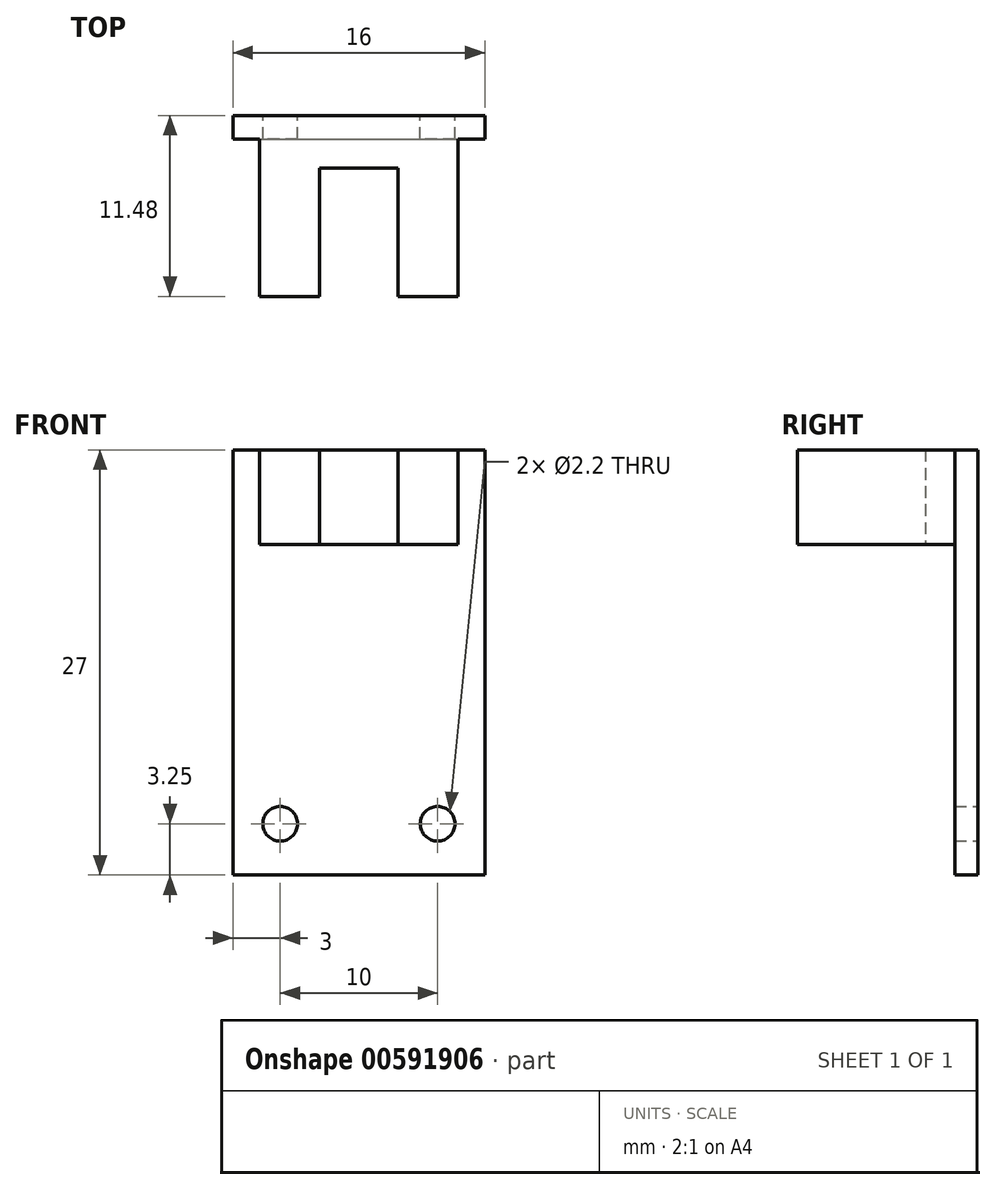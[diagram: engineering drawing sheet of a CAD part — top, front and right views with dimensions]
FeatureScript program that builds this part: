
annotation { "Feature Type Name" : "Feature", "Feature Type Description" : "" }
export const myFeature = defineFeature(function(context is Context, id is Id, definition is map)
    precondition{}
    {
        {
            var Q0;
            Q0=qCreatedBy(makeId("Front.planeOp"),FACE);
            var sketch = newSketch(context, id + "F0", { "sketchPlane" : qUnion([Q0])});
            skLineSegment(sketch, "E0.bottom", {"start": v(0, 0) * mm, "end": v(16, 0) * mm});
            skLineSegment(sketch, "E0.top", {"start": v(0, -27) * mm, "end": v(16, -27) * mm});
            skLineSegment(sketch, "E0.left", {"start": v(0, 0) * mm, "end": v(0, -27) * mm});
            skLineSegment(sketch, "E0.right", {"start": v(16, 0) * mm, "end": v(16, -27) * mm});
            skCircle(sketch, "E1", {"center": v(3, -23.75) * mm, "radius": 1.1 * mm});
            skCircle(sketch, "E2", {"center": v(13, -23.75) * mm, "radius": 1.1 * mm});
            skPoint(sketch, "E3", {"position": v(8, -27) * mm});
            skLineSegment(sketch, "E4", {"start": v(3, -23.75) * mm, "end": v(13, -23.75) * mm, "construction": true});
            skPoint(sketch, "E5", {"position": v(8, -23.75) * mm});
            skSolve(sketch);
        }
        {
            var Q0;
            Q0=makeQuery(id+"F0.imprint","IMPRINT",FACE,{"disambiguationData":[TD([[makeQuery(id+"F0.imprint","IMPRINT",EDGE,{"derivedFrom":sQuery(id+"F0.wireOp",EDGE,"E0.bottom")}),-1.0]])]});
            extrude(context, id + "F1", {"entities" : qUnion([Q0]), "depth" : 1.48 * mm, "offsetDistance" : 25 * mm});
        }
        {
            var Q0;
            Q0=makeQuery(id+"F1.opExtrude","CAP_FACE",FACE,{"disambiguationData":[OSD([sQuery(id+"F0.wireOp",EDGE,"E0.bottom"),sQuery(id+"F0.wireOp",EDGE,"E0.top"),sQuery(id+"F0.wireOp",EDGE,"E0.left"),sQuery(id+"F0.wireOp",EDGE,"E0.right")])],"isStart":false});
            var sketch = newSketch(context, id + "F2", { "sketchPlane" : qUnion([Q0])});
            skSolve(sketch);
        }
        {
            var Q0;
            Q0=makeQuery(id+"F2.imprint","IMPRINT",FACE,{"disambiguationData":[TD([[makeQuery(id+"F2.imprint","IMPRINT",EDGE,{"derivedFrom":makeQuery(id+"F1.opExtrude","CAP_EDGE",EDGE,{"disambiguationData":[OSD([sQuery(id+"F0.wireOp",EDGE,"E0.bottom")])],"isStart":false})}),-1.0]])]});
            var sketch = newSketch(context, id + "F3", { "sketchPlane" : qUnion([Q0])});
            skLineSegment(sketch, "E6.bottom", {"start": v(1.7, 0) * mm, "end": v(14.3, 0) * mm});
            skLineSegment(sketch, "E6.top", {"start": v(1.7, -6) * mm, "end": v(14.3, -6) * mm});
            skLineSegment(sketch, "E6.left", {"start": v(1.7, 0) * mm, "end": v(1.7, -6) * mm});
            skLineSegment(sketch, "E6.right", {"start": v(14.3, 0) * mm, "end": v(14.3, -6) * mm});
            skLineSegment(sketch, "E7", {"start": v(5.5, 0) * mm, "end": v(5.5, -6) * mm});
            skLineSegment(sketch, "E8", {"start": v(10.5, 0) * mm, "end": v(10.5, -6) * mm});
            skPoint(sketch, "E9", {"position": v(8, 0) * mm});
            skLineSegment(sketch, "E10.0", {"start": v(0, 0) * mm, "end": v(16, 0) * mm, "construction": true});
            skSolve(sketch);
        }
        {
            var Q0;
            {var subQ0=sQuery(id+"F3.wireOp",EDGE,"E6.left");Q0=makeQuery(id+"F3.imprint","IMPRINT",FACE,{"disambiguationData":[TD([[makeQuery(id+"F3.imprint","IMPRINT",EDGE,{"derivedFrom":subQ0}),1.0]])]});}
            var Q1;
            {var subQ0=sQuery(id+"F3.wireOp",EDGE,"E6.right");Q1=makeQuery(id+"F3.imprint","IMPRINT",FACE,{"disambiguationData":[TD([[makeQuery(id+"F3.imprint","IMPRINT",EDGE,{"derivedFrom":subQ0}),-1.0]])]});}
            extrude(context, id + "F4", {"entities" : qUnion([Q0, Q1]), "operationType" : NewBodyOperationType.ADD, "depth" : 10 * mm, "offsetDistance" : 25 * mm});
        }
        {
            var Q0;
            {var subQ0=sQuery(id+"F3.wireOp",EDGE,"E7");Q0=makeQuery(id+"F3.imprint","IMPRINT",FACE,{"disambiguationData":[TD([[makeQuery(id+"F3.imprint","IMPRINT",EDGE,{"derivedFrom":subQ0}),1.0]])]});}
            extrude(context, id + "F5", {"entities" : qUnion([Q0]), "operationType" : NewBodyOperationType.ADD, "depth" : 1.85 * mm, "offsetDistance" : 25 * mm});
        }
    });
